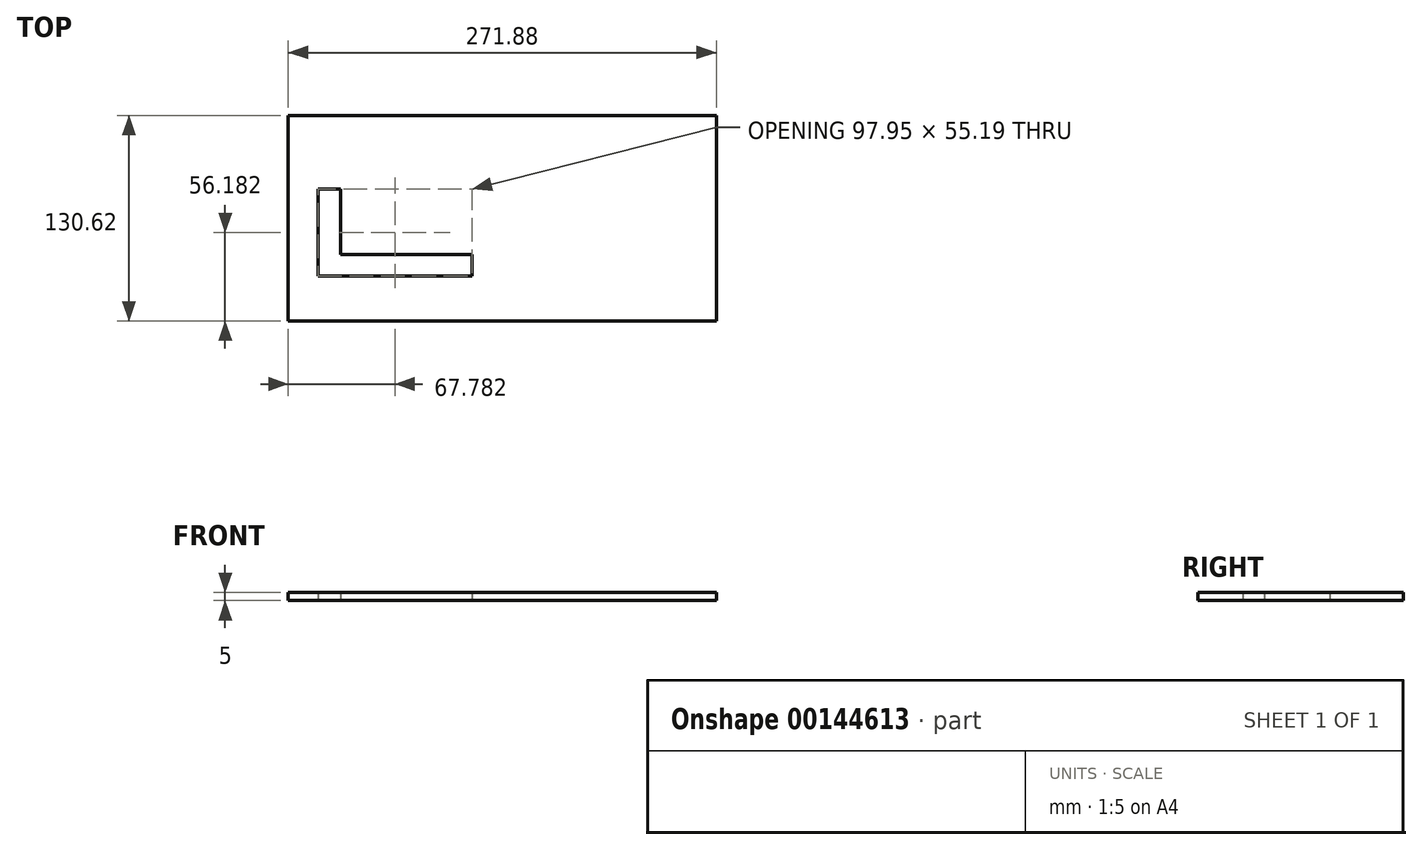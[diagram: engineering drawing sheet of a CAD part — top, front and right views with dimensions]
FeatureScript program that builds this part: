
annotation { "Feature Type Name" : "Feature", "Feature Type Description" : "" }
export const myFeature = defineFeature(function(context is Context, id is Id, definition is map)
    precondition{}
    {
        {
            var Q0;
            Q0=qCreatedBy(makeId("Top.planeOp"),FACE);
            var sketch = newSketch(context, id + "F0", { "sketchPlane" : qUnion([Q0])});
            skLineSegment(sketch, "E0.bottom", {"start": v(-142.59, 66.51) * mm, "end": v(129.3, 66.51) * mm});
            skLineSegment(sketch, "E0.top", {"start": v(-142.59, -64.11) * mm, "end": v(129.3, -64.11) * mm});
            skLineSegment(sketch, "E0.left", {"start": v(-142.59, 66.51) * mm, "end": v(-142.59, -64.11) * mm});
            skLineSegment(sketch, "E0.right", {"start": v(129.3, 66.51) * mm, "end": v(129.3, -64.11) * mm});
            skLineSegment(sketch, "E1", {"start": v(-123.78, 19.67) * mm, "end": v(-123.78, -35.52) * mm});
            skLineSegment(sketch, "E2", {"start": v(-123.78, -35.52) * mm, "end": v(-25.83, -35.52) * mm});
            skLineSegment(sketch, "E3", {"start": v(-25.83, -35.52) * mm, "end": v(-25.83, -22) * mm});
            skLineSegment(sketch, "E4", {"start": v(-25.83, -22) * mm, "end": v(-109.34, -22) * mm});
            skLineSegment(sketch, "E5", {"start": v(-109.34, -22) * mm, "end": v(-109.34, 19.67) * mm});
            skLineSegment(sketch, "E6", {"start": v(-109.34, 19.67) * mm, "end": v(-123.78, 19.67) * mm});
            skSolve(sketch);
        }
        {
            var Q0;
            Q0=makeQuery(id+"F0.imprint","IMPRINT",FACE,{"disambiguationData":[TD([[makeQuery(id+"F0.imprint","IMPRINT",EDGE,{"derivedFrom":sQuery(id+"F0.wireOp",EDGE,"E0.bottom")}),-1.0]])]});
            extrude(context, id + "F1", {"entities" : qUnion([Q0]), "depth" : 5 * mm});
        }
    });
